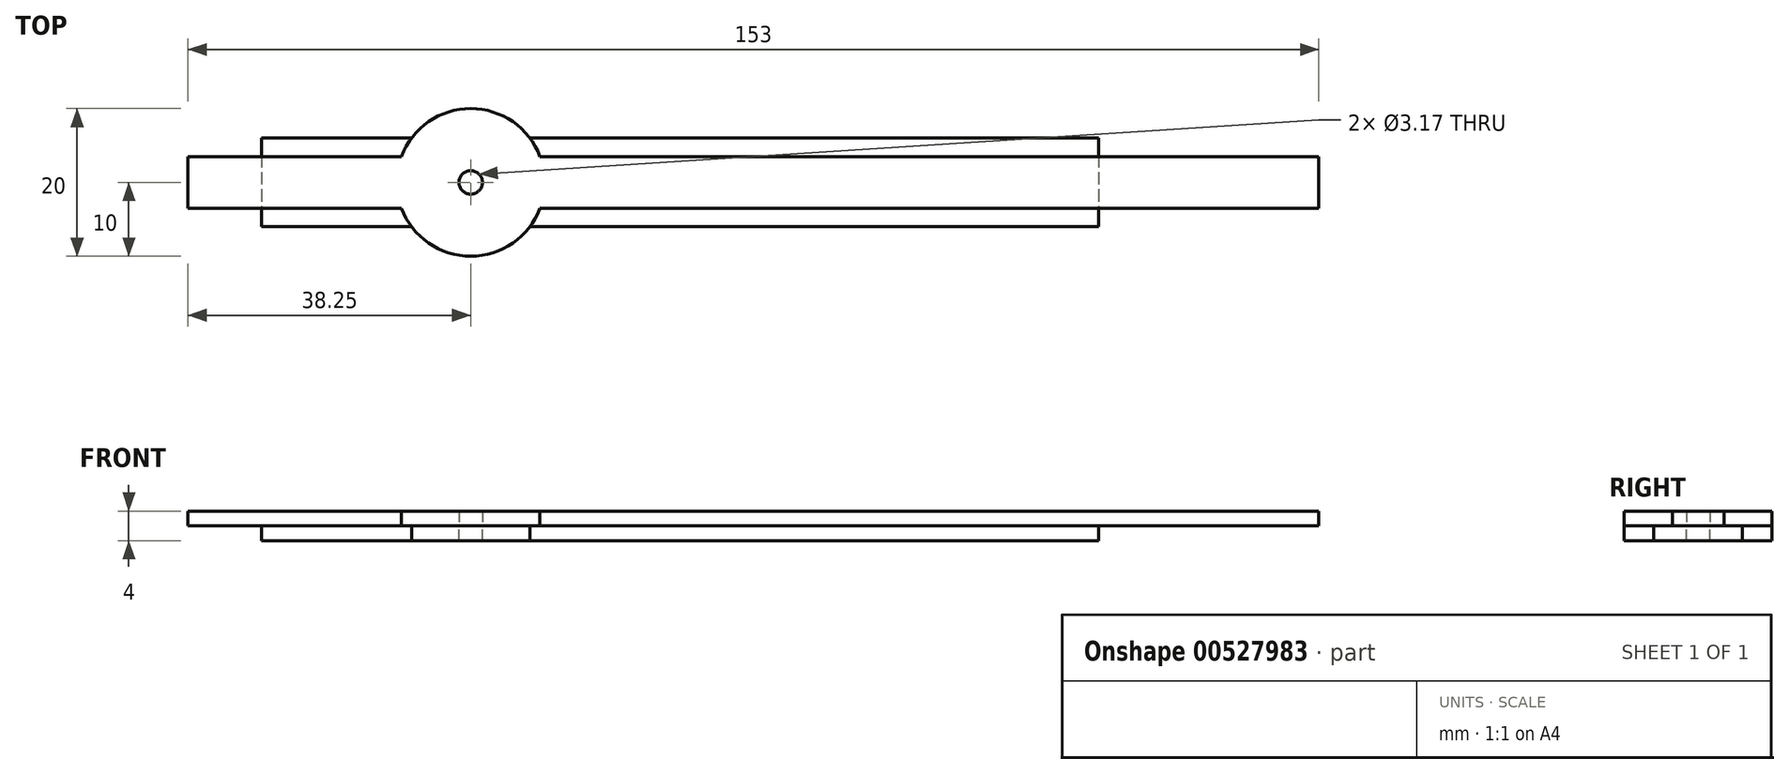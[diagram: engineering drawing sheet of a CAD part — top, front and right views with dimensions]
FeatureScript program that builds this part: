
annotation { "Feature Type Name" : "Feature", "Feature Type Description" : "" }
export const myFeature = defineFeature(function(context is Context, id is Id, definition is map)
    precondition{}
    {
        {
            var Q0;
            Q0=qCreatedBy(makeId("Top.planeOp"),FACE);
            var sketch = newSketch(context, id + "F0", { "sketchPlane" : qUnion([Q0])});
            skCircle(sketch, "E0", {"center": v(0, 0) * mm, "radius": 1.59 * mm});
            skLineSegment(sketch, "E1.bottom", {"start": v(-38.25, 3.5) * mm, "end": v(114.75, 3.5) * mm});
            skLineSegment(sketch, "E1.top", {"start": v(-38.25, -3.5) * mm, "end": v(114.75, -3.5) * mm});
            skLineSegment(sketch, "E1.left", {"start": v(-38.25, 3.5) * mm, "end": v(-38.25, -3.5) * mm});
            skLineSegment(sketch, "E1.right", {"start": v(114.75, 3.5) * mm, "end": v(114.75, -3.5) * mm});
            skCircle(sketch, "E2", {"center": v(0, 0) * mm, "radius": 10 * mm});
            skSolve(sketch);
        }
        {
            var Q0;
            Q0=qSketchRegion(id+"F0",true);
            extrude(context, id + "F1", {"entities" : qUnion([Q0]), "depth" : 2 * mm});
        }
        {
            var Q0;
            Q0=qCreatedBy(makeId("Top.planeOp"),FACE);
            var sketch = newSketch(context, id + "F2", { "sketchPlane" : qUnion([Q0])});
            skCircle(sketch, "E3", {"center": v(0, 0) * mm, "radius": 1.59 * mm});
            skLineSegment(sketch, "E4.bottom", {"start": v(-28.33, 6) * mm, "end": v(85, 6) * mm});
            skLineSegment(sketch, "E4.top", {"start": v(-28.33, -6) * mm, "end": v(85, -6) * mm});
            skLineSegment(sketch, "E4.left", {"start": v(-28.33, 6) * mm, "end": v(-28.33, -6) * mm});
            skLineSegment(sketch, "E4.right", {"start": v(85, 6) * mm, "end": v(85, -6) * mm});
            skCircle(sketch, "E5", {"center": v(0, 0) * mm, "radius": 10 * mm});
            skSolve(sketch);
        }
        {
            var Q0;
            Q0=qSketchRegion(id+"F2",true);
            extrude(context, id + "F3", {"entities" : qUnion([Q0]), "oppositeDirection" : true, "depth" : 2 * mm});
        }
    });
